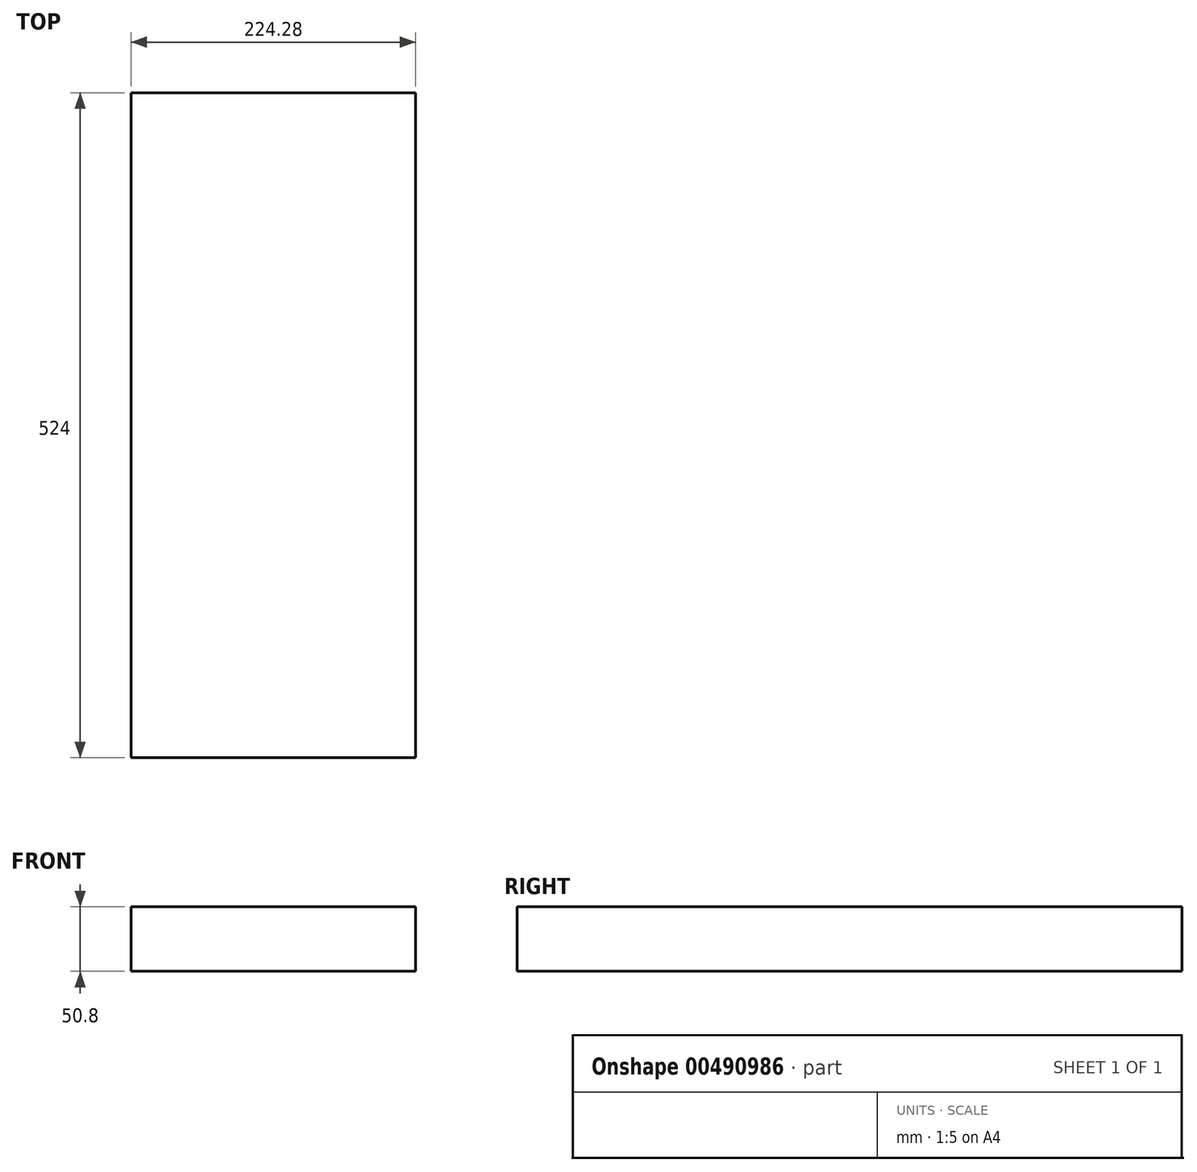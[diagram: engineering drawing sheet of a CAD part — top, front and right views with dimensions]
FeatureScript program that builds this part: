
annotation { "Feature Type Name" : "Feature", "Feature Type Description" : "" }
export const myFeature = defineFeature(function(context is Context, id is Id, definition is map)
    precondition{}
    {
        {
            var Q0;
            Q0=qCreatedBy(makeId("Top.planeOp"),FACE);
            var sketch = newSketch(context, id + "F0", { "sketchPlane" : qUnion([Q0])});
            skLineSegment(sketch, "E0.bottom", {"start": v(-112.14, 262) * mm, "end": v(112.14, 262) * mm});
            skLineSegment(sketch, "E0.top", {"start": v(-112.14, -262) * mm, "end": v(112.14, -262) * mm});
            skLineSegment(sketch, "E0.left", {"start": v(-112.14, 262) * mm, "end": v(-112.14, -262) * mm});
            skLineSegment(sketch, "E0.right", {"start": v(112.14, 262) * mm, "end": v(112.14, -262) * mm});
            skPoint(sketch, "E0.middle", {"position": v(0, 0) * mm});
            skSolve(sketch);
        }
        {
            var Q0;
            Q0=makeQuery(id+"F0.imprint","IMPRINT",FACE,{"disambiguationData":[TD([[makeQuery(id+"F0.imprint","IMPRINT",EDGE,{"derivedFrom":sQuery(id+"F0.wireOp",EDGE,"E0.bottom")}),-1.0]])]});
            extrude(context, id + "F1", {"entities" : qUnion([Q0]), "depth" : 50.8 * mm});
        }
    });
